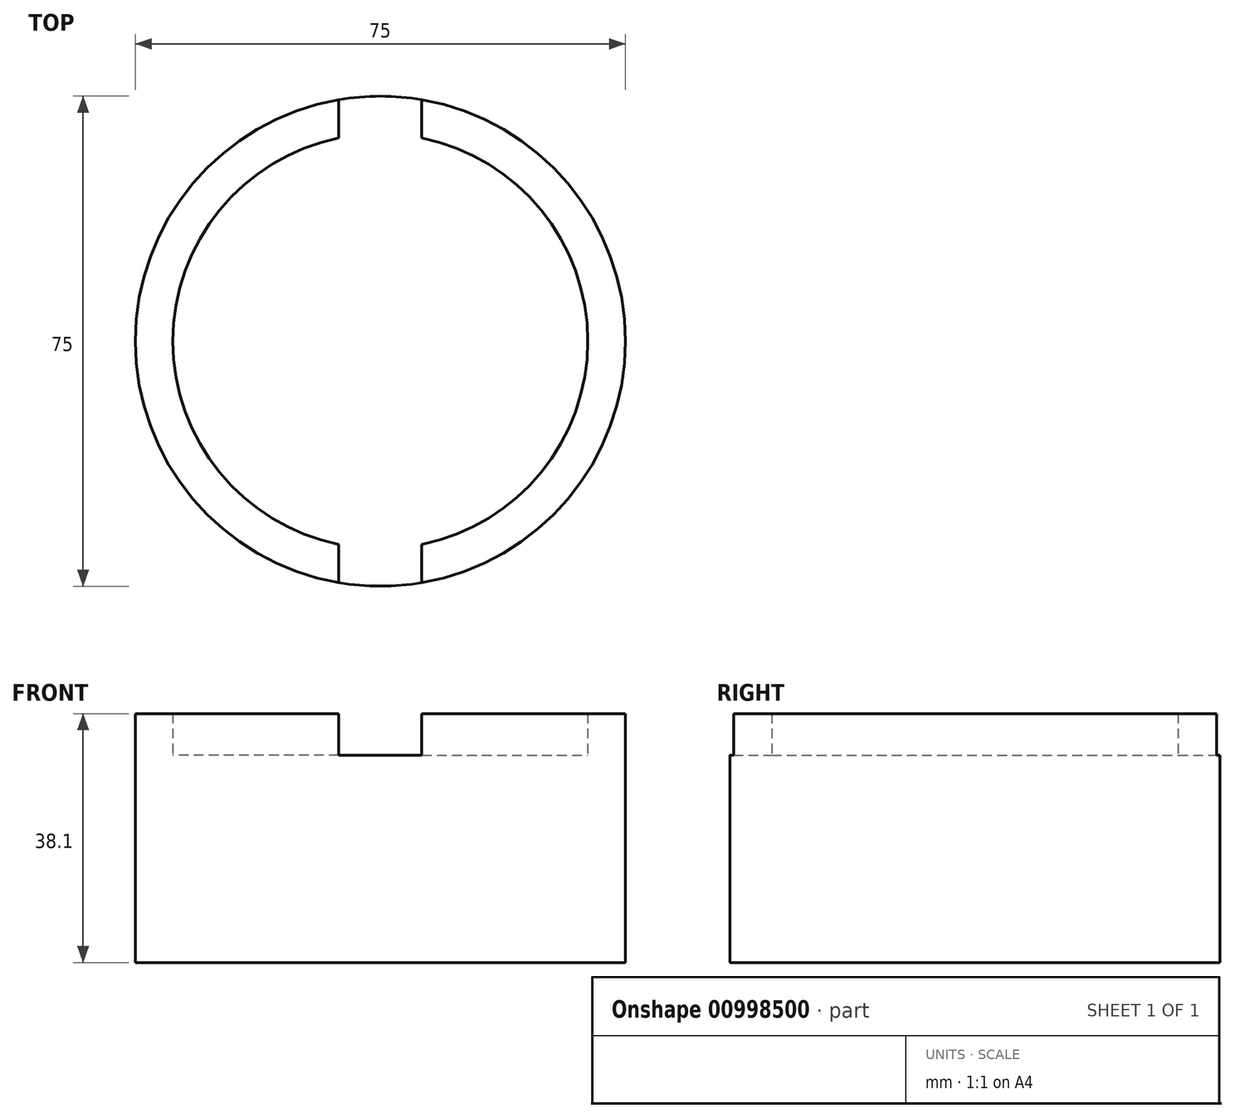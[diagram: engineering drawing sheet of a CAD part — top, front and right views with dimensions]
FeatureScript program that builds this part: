
annotation { "Feature Type Name" : "Feature", "Feature Type Description" : "" }
export const myFeature = defineFeature(function(context is Context, id is Id, definition is map)
    precondition{}
    {
        {
            var Q0;
            Q0=qCreatedBy(makeId("Top.planeOp"),FACE);
            var sketch = newSketch(context, id + "F0", { "sketchPlane" : qUnion([Q0])});
            skCircle(sketch, "E0", {"center": v(0, 0) * mm, "radius": 37.5 * mm});
            skSolve(sketch);
        }
        {
            var Q0;
            Q0=makeQuery(id+"F0.imprint","IMPRINT",FACE,{"disambiguationData":[TD([[makeQuery(id+"F0.imprint","IMPRINT",EDGE,{"derivedFrom":sQuery(id+"F0.wireOp",EDGE,"E0")}),1.0]])]});
            extrude(context, id + "F1", {"entities" : qUnion([Q0]), "depth" : 38.1 * mm, "offsetDistance" : 25.4 * mm});
        }
        {
            var Q0;
            Q0=qCreatedBy(makeId("Front.planeOp"),FACE);
            var sketch = newSketch(context, id + "F2", { "sketchPlane" : qUnion([Q0])});
            skLineSegment(sketch, "E1.bottom", {"start": v(-6.35, 44.45) * mm, "end": v(6.35, 44.45) * mm});
            skLineSegment(sketch, "E1.top", {"start": v(-6.35, 31.75) * mm, "end": v(6.35, 31.75) * mm});
            skLineSegment(sketch, "E1.left", {"start": v(-6.35, 44.45) * mm, "end": v(-6.35, 31.75) * mm});
            skLineSegment(sketch, "E1.right", {"start": v(6.35, 44.45) * mm, "end": v(6.35, 31.75) * mm});
            skSolve(sketch);
        }
        {
            var Q0;
            Q0=makeQuery(id+"F2.imprint","IMPRINT",FACE,{"disambiguationData":[TD([[makeQuery(id+"F2.imprint","IMPRINT",EDGE,{"derivedFrom":sQuery(id+"F2.wireOp",EDGE,"E1.bottom")}),-1.0]])]});
            extrude(context, id + "F3", {"entities" : qUnion([Q0]), "operationType" : NewBodyOperationType.REMOVE, "endBound" : BoundingType.THROUGH_ALL, "depth" : 25.4 * mm, "hasOffset" : true, "offsetDistance" : 12.7 * mm, "hasSecondDirection" : true, "secondDirectionBound" : SecondDirectionBoundingType.THROUGH_ALL, "secondDirectionOppositeDirection" : true, "secondDirectionDepth" : 25.4 * mm});
        }
        {
            var Q0;
            Q0=qCreatedBy(makeId("Right.planeOp"),FACE);
            var sketch = newSketch(context, id + "F4", { "sketchPlane" : qUnion([Q0])});
            skLineSegment(sketch, "E2", {"start": v(0, 76.9) * mm, "end": v(0, -56.28) * mm, "construction": true});
            skSolve(sketch);
        }
        {
            var Q0;
            {var subQ0=sQuery(id+"F2.wireOp",EDGE,"E1.top");Q0=makeQuery(id+"Fda7QvrxMJNmx3A_1.4.F3.boolean.opBoolean","MERGE",FACE,{"derivedFrom":[makeQuery(id+"Fda7QvrxMJNmx3A_1.3.F3.boolean.opBoolean","MERGE",FACE,{"derivedFrom":[makeQuery(id+"Fda7QvrxMJNmx3A_1.2.F3.boolean.opBoolean","MERGE",FACE,{"derivedFrom":[makeQuery(id+"Fda7QvrxMJNmx3A_1.1.F3.boolean.opBoolean","MERGE",FACE,{"derivedFrom":[makeQuery(id+"F3.boolean.opBoolean","COPY",FACE,{"derivedFrom":makeQuery(id+"F3.opExtrude","SWEPT_FACE",FACE,{"disambiguationData":[OSD([subQ0])]})})],"fromTools":[makeQuery(id+"Fda7QvrxMJNmx3A_1.1.F3.opExtrude","SWEPT_FACE",FACE,{"disambiguationData":[OSD([subQ0])]})]})],"fromTools":[makeQuery(id+"Fda7QvrxMJNmx3A_1.2.F3.opExtrude","SWEPT_FACE",FACE,{"disambiguationData":[OSD([subQ0])]})]})],"fromTools":[makeQuery(id+"Fda7QvrxMJNmx3A_1.3.F3.opExtrude","SWEPT_FACE",FACE,{"disambiguationData":[OSD([subQ0])]})]})],"fromTools":[makeQuery(id+"Fda7QvrxMJNmx3A_1.4.F3.opExtrude","SWEPT_FACE",FACE,{"disambiguationData":[OSD([subQ0])]})]});}
            var sketch = newSketch(context, id + "F5", { "sketchPlane" : qUnion([Q0])});
            skCircle(sketch, "E3", {"center": v(0, 0) * mm, "radius": 31.75 * mm});
            skSolve(sketch);
        }
        {
            var Q0;
            Q0 = qSketchRegion(id + "F5", true);
            extrude(context, id + "F6", {"entities" : qUnion([Q0]), "operationType" : NewBodyOperationType.REMOVE, "endBound" : BoundingType.THROUGH_ALL, "depth" : 25.4 * mm, "offsetDistance" : 25.4 * mm});
        }
    });
